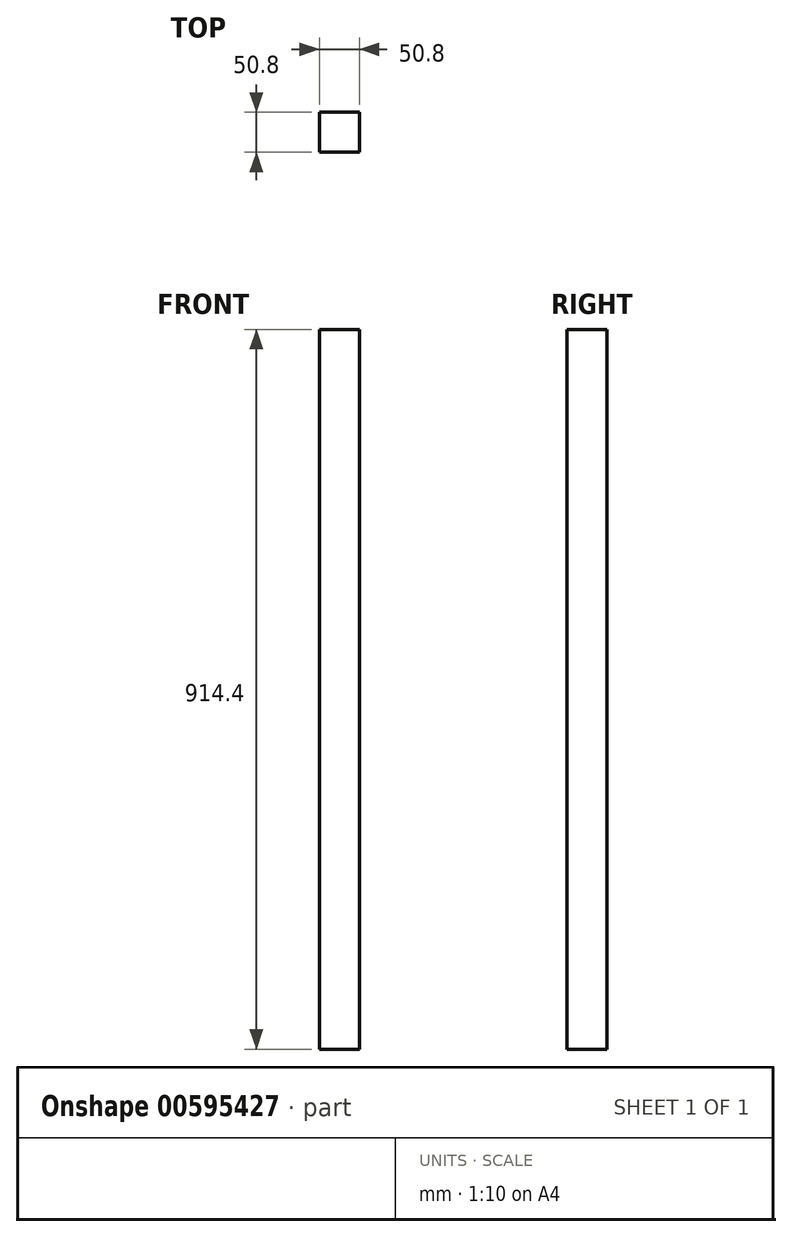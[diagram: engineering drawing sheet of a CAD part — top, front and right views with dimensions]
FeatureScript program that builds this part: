
annotation { "Feature Type Name" : "Feature", "Feature Type Description" : "" }
export const myFeature = defineFeature(function(context is Context, id is Id, definition is map)
    precondition{}
    {
        {
            var Q0;
            Q0=qCreatedBy(makeId("Top.planeOp"),FACE);
            var sketch = newSketch(context, id + "F0", { "sketchPlane" : qUnion([Q0])});
            skLineSegment(sketch, "E0.bottom", {"start": v(-203.2, -203.6) * mm, "end": v(-254, -203.6) * mm});
            skLineSegment(sketch, "E0.top", {"start": v(-203.2, -254.4) * mm, "end": v(-254, -254.4) * mm});
            skLineSegment(sketch, "E0.left", {"start": v(-203.2, -203.6) * mm, "end": v(-203.2, -254.4) * mm});
            skLineSegment(sketch, "E0.right", {"start": v(-254, -203.6) * mm, "end": v(-254, -254.4) * mm});
            skSolve(sketch);
        }
        {
            var Q0;
            Q0=makeQuery(id+"F0.imprint","IMPRINT",FACE,{"disambiguationData":[TD([[makeQuery(id+"F0.imprint","IMPRINT",EDGE,{"derivedFrom":sQuery(id+"F0.wireOp",EDGE,"E0.bottom")}),1.0]])]});
            extrude(context, id + "F1", {"entities" : qUnion([Q0]), "depth" : 914.4 * mm, "offsetDistance" : 25.4 * mm});
        }
    });
